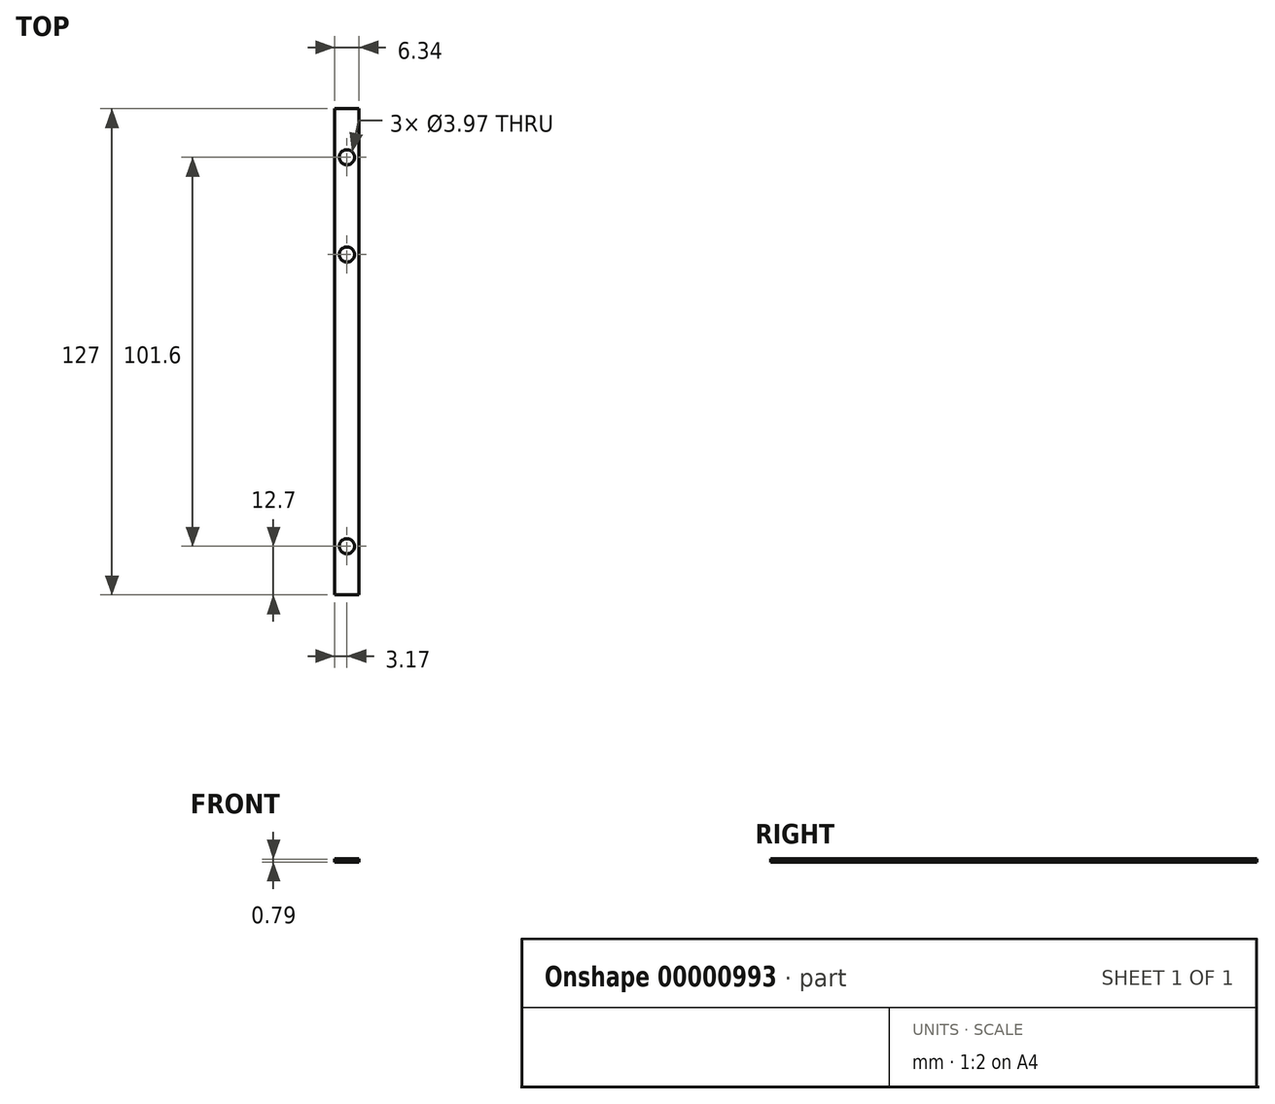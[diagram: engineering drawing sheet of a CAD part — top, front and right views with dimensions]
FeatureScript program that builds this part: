
annotation { "Feature Type Name" : "Feature", "Feature Type Description" : "" }
export const myFeature = defineFeature(function(context is Context, id is Id, definition is map)
    precondition{}
    {
        {
            var Q0;
            Q0=qCreatedBy(makeId("Top.planeOp"),FACE);
            var sketch = newSketch(context, id + "F0", { "sketchPlane" : qUnion([Q0])});
            skLineSegment(sketch, "E0.rect.bottom", {"start": v(3.17, 63.5) * mm, "end": v(-3.18, 63.5) * mm});
            skLineSegment(sketch, "E0.rect.top", {"start": v(3.17, -63.5) * mm, "end": v(-3.18, -63.5) * mm});
            skLineSegment(sketch, "E0.rect.left", {"start": v(3.17, 63.5) * mm, "end": v(3.17, -63.5) * mm});
            skLineSegment(sketch, "E0.rect.right", {"start": v(-3.18, 63.5) * mm, "end": v(-3.18, -63.5) * mm});
            skPoint(sketch, "E0.rect.middle", {"position": v(0, 0) * mm});
            skCircle(sketch, "E1", {"center": v(0, 50.8) * mm, "radius": 1.98 * mm});
            skCircle(sketch, "E2", {"center": v(0, -50.8) * mm, "radius": 1.98 * mm});
            skCircle(sketch, "E3", {"center": v(0, 25.4) * mm, "radius": 1.98 * mm});
            skSolve(sketch);
        }
        {
            var Q0;
            Q0=makeQuery(id+"F0.imprint","IMPRINT",FACE,{"disambiguationData":[TD([[makeQuery(id+"F0.imprint","IMPRINT",EDGE,{"derivedFrom":sQuery(id+"F0.wireOp",EDGE,"E0.rect.bottom")}),1.0]])]});
            extrude(context, id + "F1", {"entities" : qUnion([Q0]), "depth" : 0.8 * mm});
        }
    });
